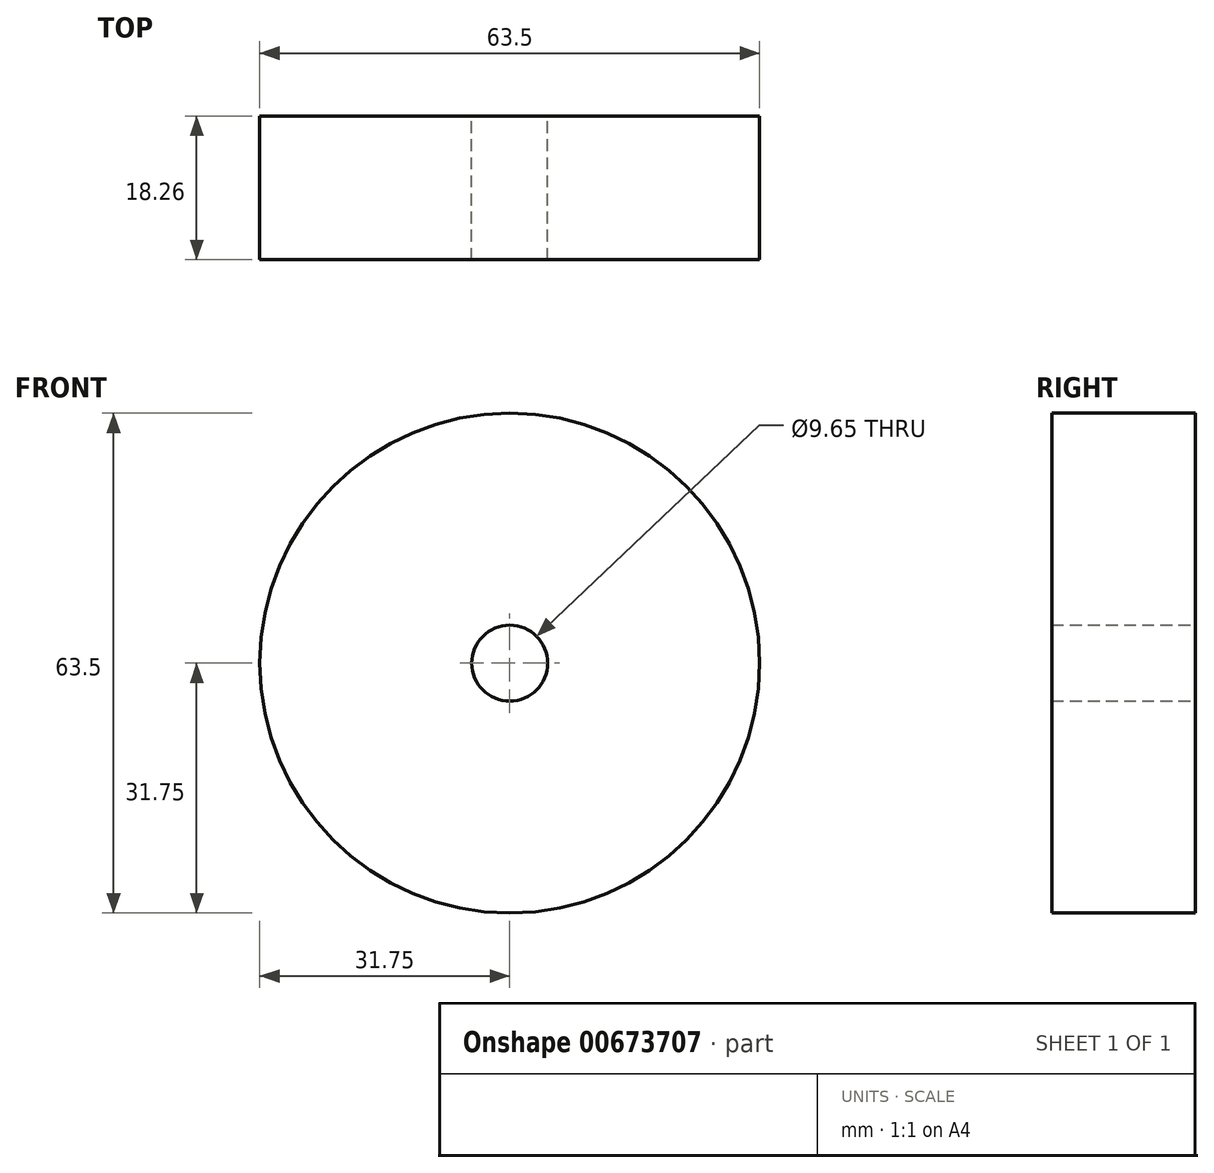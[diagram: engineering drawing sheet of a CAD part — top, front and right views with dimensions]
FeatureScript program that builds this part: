
annotation { "Feature Type Name" : "Feature", "Feature Type Description" : "" }
export const myFeature = defineFeature(function(context is Context, id is Id, definition is map)
    precondition{}
    {
        {
            var Q0;
            Q0=qCreatedBy(makeId("Front.planeOp"),FACE);
            var sketch = newSketch(context, id + "F0", { "sketchPlane" : qUnion([Q0])});
            skCircle(sketch, "E0", {"center": v(0, 0) * mm, "radius": 31.75 * mm});
            skCircle(sketch, "E1", {"center": v(0, 0) * mm, "radius": 4.83 * mm});
            skSolve(sketch);
        }
        {
            var Q0;
            Q0 = qSketchRegion(id + "F0", true);
            extrude(context, id + "F1", {"entities" : qUnion([Q0]), "endBound" : BoundingType.SYMMETRIC, "depth" : 18.26 * mm, "offsetDistance" : 25.4 * mm});
        }
    });
